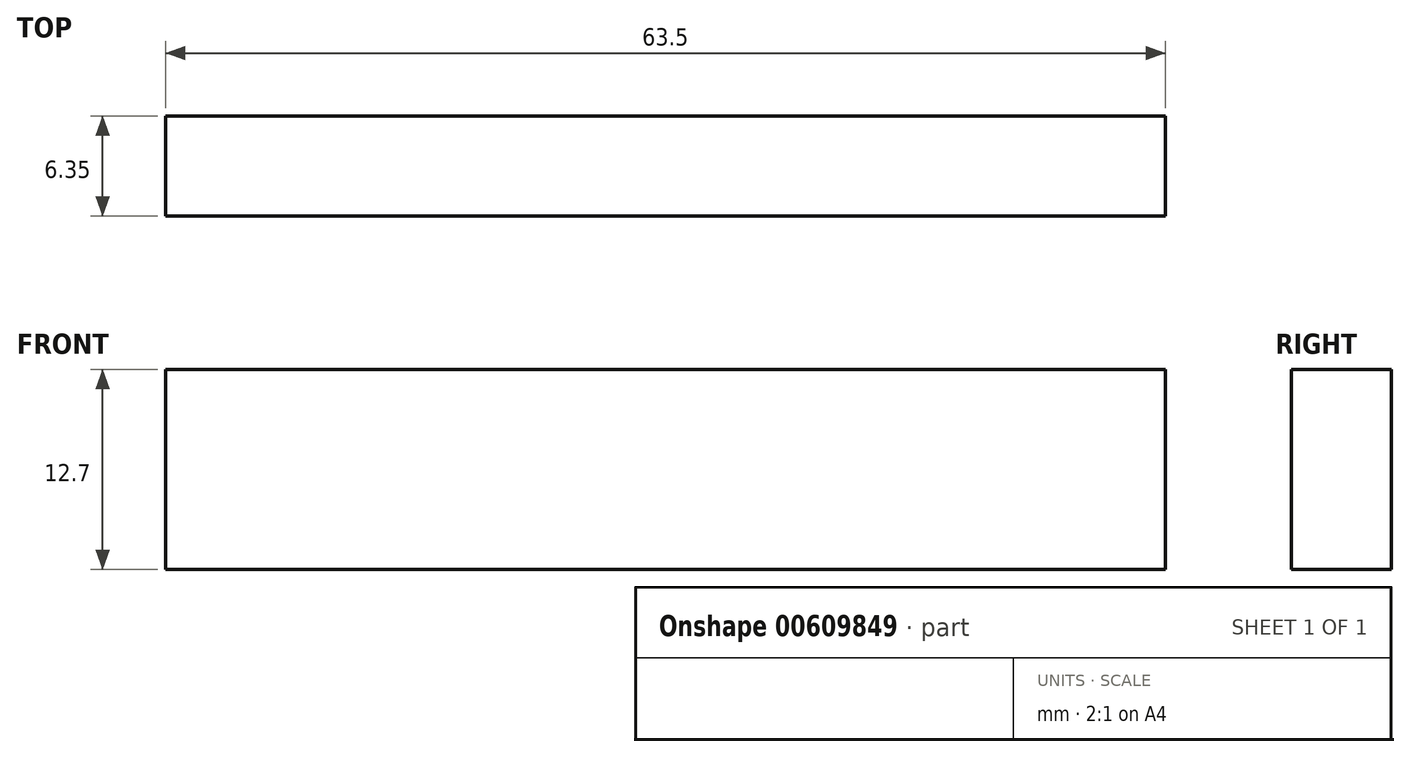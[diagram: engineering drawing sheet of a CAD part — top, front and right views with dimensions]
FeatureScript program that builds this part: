
annotation { "Feature Type Name" : "Feature", "Feature Type Description" : "" }
export const myFeature = defineFeature(function(context is Context, id is Id, definition is map)
    precondition{}
    {
        {
            var Q0;
            Q0=qCreatedBy(makeId("Front.planeOp"),FACE);
            var sketch = newSketch(context, id + "F0", { "sketchPlane" : qUnion([Q0])});
            skLineSegment(sketch, "E0.bottom", {"start": v(-4.16, -15.27) * mm, "end": v(59.34, -15.27) * mm});
            skLineSegment(sketch, "E0.top", {"start": v(-4.16, -27.97) * mm, "end": v(59.34, -27.97) * mm});
            skLineSegment(sketch, "E0.left", {"start": v(-4.16, -15.27) * mm, "end": v(-4.16, -27.97) * mm});
            skLineSegment(sketch, "E0.right", {"start": v(59.34, -15.27) * mm, "end": v(59.34, -27.97) * mm});
            skCircle(sketch, "E1", {"center": v(-62.19, 41.24) * mm, "radius": 3.18 * mm});
            skSolve(sketch);
        }
        {
            var Q0;
            Q0=makeQuery(id+"F0.imprint","IMPRINT",FACE,{"disambiguationData":[TD([[makeQuery(id+"F0.imprint","IMPRINT",EDGE,{"derivedFrom":sQuery(id+"F0.wireOp",EDGE,"E0.bottom")}),-1.0]])]});
            extrude(context, id + "F1", {"entities" : qUnion([Q0]), "depth" : 6.35 * mm, "offsetDistance" : 25.4 * mm});
        }
    });
